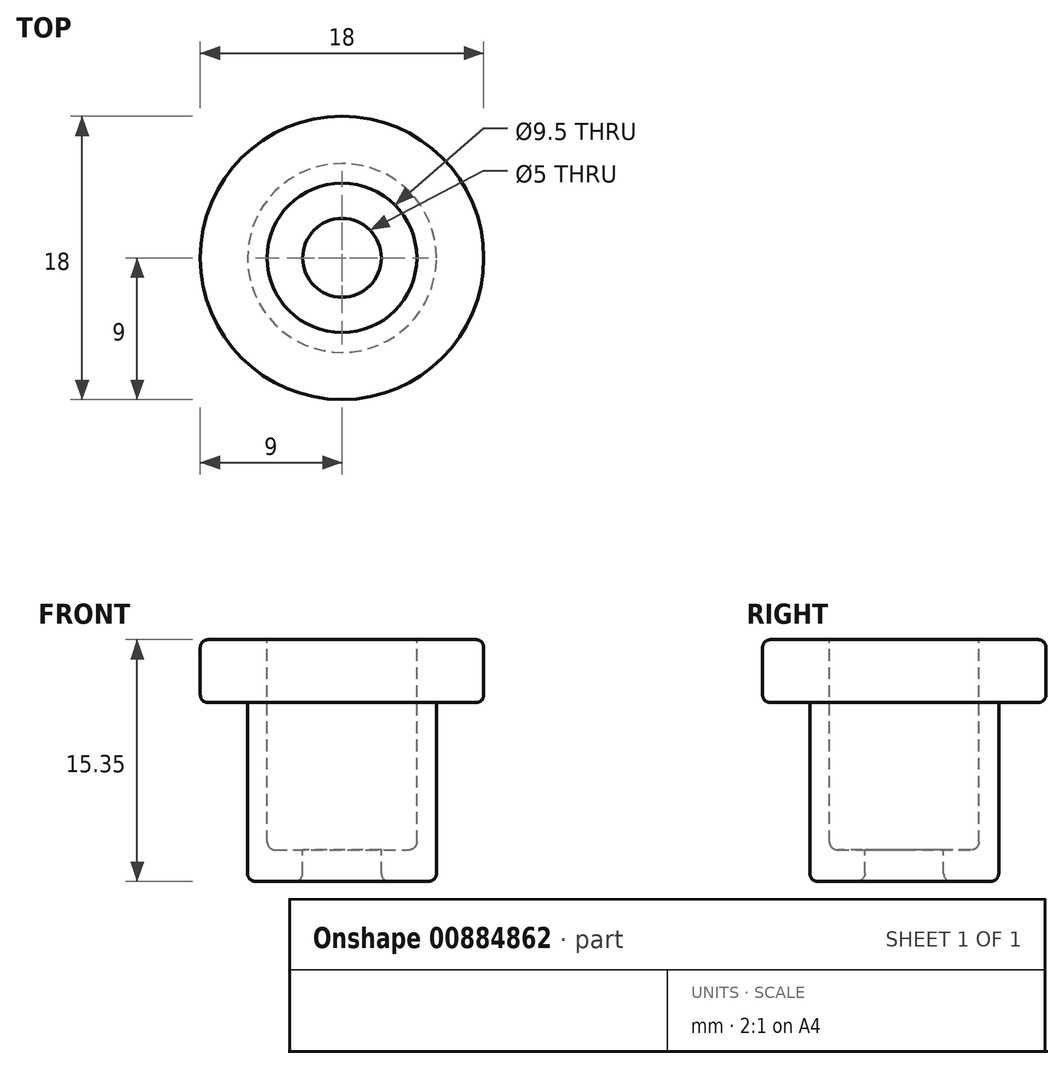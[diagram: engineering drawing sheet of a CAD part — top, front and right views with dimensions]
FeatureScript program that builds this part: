
annotation { "Feature Type Name" : "Feature", "Feature Type Description" : "" }
export const myFeature = defineFeature(function(context is Context, id is Id, definition is map)
    precondition{}
    {
        {
            var Q0;
            Q0=qCreatedBy(makeId("Top.planeOp"),FACE);
            var sketch = newSketch(context, id + "F0", { "sketchPlane" : qUnion([Q0])});
            skCircle(sketch, "E0", {"center": v(0, 0) * mm, "radius": 9 * mm});
            skSolve(sketch);
        }
        {
            var Q0;
            Q0 = qSketchRegion(id + "F0", true);
            extrude(context, id + "F1", {"entities" : qUnion([Q0]), "depth" : 4 * mm, "offsetDistance" : 25 * mm});
        }
        {
            var Q0;
            Q0=makeQuery(id+"F1.opExtrude","CAP_FACE",FACE,{"disambiguationData":[OSD([sQuery(id+"F0.wireOp",EDGE,"E0")])],"isStart":true});
            var sketch = newSketch(context, id + "F2", { "sketchPlane" : qUnion([Q0])});
            skCircle(sketch, "E1", {"center": v(0, 0) * mm, "radius": 6 * mm});
            skSolve(sketch);
        }
        {
            var Q0;
            Q0 = qSketchRegion(id + "F2", true);
            extrude(context, id + "F3", {"entities" : qUnion([Q0]), "operationType" : NewBodyOperationType.ADD, "depth" : (6.35 + 5) * mm, "offsetDistance" : 25 * mm});
        }
        {
            var Q0;
            Q0=makeQuery(id+"F1.opExtrude","CAP_FACE",FACE,{"disambiguationData":[OSD([sQuery(id+"F0.wireOp",EDGE,"E0")])],"isStart":false});
            var sketch = newSketch(context, id + "F4", { "sketchPlane" : qUnion([Q0])});
            skCircle(sketch, "E2.0", {"center": v(0, 0) * mm, "radius": 9 * mm});
            skCircle(sketch, "E3.0", {"center": v(0, 0) * mm, "radius": 9 * mm, "construction": true});
            skCircle(sketch, "E4", {"center": v(0, 0) * mm, "radius": 4.75 * mm});
            skSolve(sketch);
        }
        {
            var Q0;
            Q0=makeQuery(id+"F4.imprint","IMPRINT",FACE,{"disambiguationData":[TD([[makeQuery(id+"F4.imprint","IMPRINT",EDGE,{"derivedFrom":sQuery(id+"F4.wireOp",EDGE,"E4")}),1.0]])]});
            var Q1;
            Q1=makeQuery(id+"F3.opExtrude","CAP_FACE",FACE,{"disambiguationData":[OSD([sQuery(id+"F2.wireOp",EDGE,"E1")])],"isStart":false});
            extrude(context, id + "F5", {"entities" : qUnion([Q0]), "operationType" : NewBodyOperationType.REMOVE, "endBound" : BoundingType.UP_TO_SURFACE, "oppositeDirection" : true, "depth" : 9 * mm, "endBoundEntityFace" : qUnion([Q1]), "hasOffset" : true, "offsetDistance" : 2 * mm});
        }
        {
            var Q0;
            Q0=makeQuery(id+"F1.opExtrude","CAP_EDGE",EDGE,{"disambiguationData":[OSD([sQuery(id+"F0.wireOp",EDGE,"E0")])],"isStart":false});
            var Q1;
            Q1=makeQuery(id+"F3.opExtrude","CAP_EDGE",EDGE,{"disambiguationData":[OSD([sQuery(id+"F2.wireOp",EDGE,"E1")])],"isStart":true});
            var Q2;
            Q2=makeQuery(id+"F1.opExtrude","CAP_EDGE",EDGE,{"disambiguationData":[OSD([sQuery(id+"F0.wireOp",EDGE,"E0")])],"isStart":true});
            var Q3;
            Q3=makeQuery(id+"FszR8cdfjDlN7IH_1.opChamfer","BLEND_EDGE",EDGE,{"blendedFrom":[makeQuery(id+"F5.boolean.opBoolean","COPY",EDGE,{"derivedFrom":makeQuery(id+"F5.opExtrude","CAP_EDGE",EDGE,{"disambiguationData":[OSD([sQuery(id+"F4.wireOp",EDGE,"E4")])],"isStart":true})}),makeQuery(id+"F1.opExtrude","CAP_FACE",FACE,{"disambiguationData":[OSD([sQuery(id+"F0.wireOp",EDGE,"E0")])],"isStart":false})],"blendedInto":[makeQuery(id+"F1.opExtrude","CAP_FACE",FACE,{"disambiguationData":[OSD([sQuery(id+"F0.wireOp",EDGE,"E0")])],"isStart":false})]});
            var Q4;
            {var subQ0=sQuery(id+"F4.wireOp",EDGE,"E4");Q4=makeQuery(id+"FszR8cdfjDlN7IH_1.opChamfer","BLEND_EDGE",EDGE,{"blendedFrom":[makeQuery(id+"F5.boolean.opBoolean","COPY",EDGE,{"derivedFrom":makeQuery(id+"F5.opExtrude","CAP_EDGE",EDGE,{"disambiguationData":[OSD([subQ0])],"isStart":true})}),makeQuery(id+"F5.boolean.opBoolean","COPY",FACE,{"derivedFrom":makeQuery(id+"F5.opExtrude","SWEPT_FACE",FACE,{"disambiguationData":[OSD([subQ0])]})})],"blendedInto":[makeQuery(id+"F5.boolean.opBoolean","COPY",FACE,{"derivedFrom":makeQuery(id+"F5.opExtrude","SWEPT_FACE",FACE,{"disambiguationData":[OSD([subQ0])]})})]});}
            fillet(context, id + "F6", {"entities" : qUnion([Q0, Q1, Q2, Q3, Q4]), "radius" : 0.5 * mm, "tangentPropagation" : true, "allowEdgeOverflow" : false});
        }
        {
            var Q0;
            Q0=makeQuery(id+"F5.boolean.opBoolean","COPY",FACE,{"derivedFrom":makeQuery(id+"F5.opExtrude","CAP_FACE",FACE,{"disambiguationData":[OSD([sQuery(id+"F4.wireOp",EDGE,"E4")])],"isStart":false})});
            var sketch = newSketch(context, id + "F7", { "sketchPlane" : qUnion([Q0])});
            skCircle(sketch, "E5", {"center": v(0, 0) * mm, "radius": 2.5 * mm});
            skSolve(sketch);
        }
        {
            var Q0;
            Q0 = qSketchRegion(id + "F7", true);
            extrude(context, id + "F8", {"entities" : qUnion([Q0]), "operationType" : NewBodyOperationType.REMOVE, "endBound" : BoundingType.THROUGH_ALL, "oppositeDirection" : true, "depth" : 25 * mm, "offsetDistance" : 25 * mm});
        }
        {
            var Q0;
            Q0=makeQuery(id+"F3.opExtrude","CAP_EDGE",EDGE,{"disambiguationData":[OSD([sQuery(id+"F2.wireOp",EDGE,"E1")])],"isStart":false});
            fillet(context, id + "F9", {"entities" : qUnion([Q0]), "radius" : .5 * mm, "tangentPropagation" : true, "allowEdgeOverflow" : false});
        }
        {
            var Q0;
            Q0=makeQuery(id+"F5.boolean.opBoolean","COPY",EDGE,{"derivedFrom":makeQuery(id+"F5.opExtrude","CAP_EDGE",EDGE,{"disambiguationData":[OSD([sQuery(id+"F4.wireOp",EDGE,"E4")])],"isStart":false})});
            var Q1;
            Q1=makeQuery(id+"F5.boolean.opBoolean","COPY",EDGE,{"derivedFrom":makeQuery(id+"F5.opExtrude","CAP_EDGE",EDGE,{"disambiguationData":[OSD([sQuery(id+"F4.wireOp",EDGE,"E4")])],"isStart":true})});
            fillet(context, id + "F10", {"entities" : qUnion([Q0, Q1]), "radius" : 0.5 * mm, "tangentPropagation" : true, "allowEdgeOverflow" : false});
        }
        {
            var Q0;
            Q0=makeQuery(id+"F8.boolean.opBoolean","COPY",EDGE,{"derivedFrom":makeQuery(id+"F8.opExtrude","CAP_EDGE",EDGE,{"disambiguationData":[OSD([sQuery(id+"F7.wireOp",EDGE,"E5")])],"isStart":true})});
            var Q1;
            Q1=makeQuery(id+"F8.boolean.opBoolean","INTERSECT",EDGE,{"derivedFrom":[makeQuery(id+"F3.opExtrude","CAP_FACE",FACE,{"disambiguationData":[OSD([sQuery(id+"F2.wireOp",EDGE,"E1")])],"isStart":false}),makeQuery(id+"F8.opExtrude","SWEPT_FACE",FACE,{"disambiguationData":[OSD([sQuery(id+"F7.wireOp",EDGE,"E5")])]})]});
            fillet(context, id + "F11", {"entities" : qUnion([Q0, Q1]), "radius" : 0.5 * mm, "tangentPropagation" : true, "allowEdgeOverflow" : false});
        }
    });
